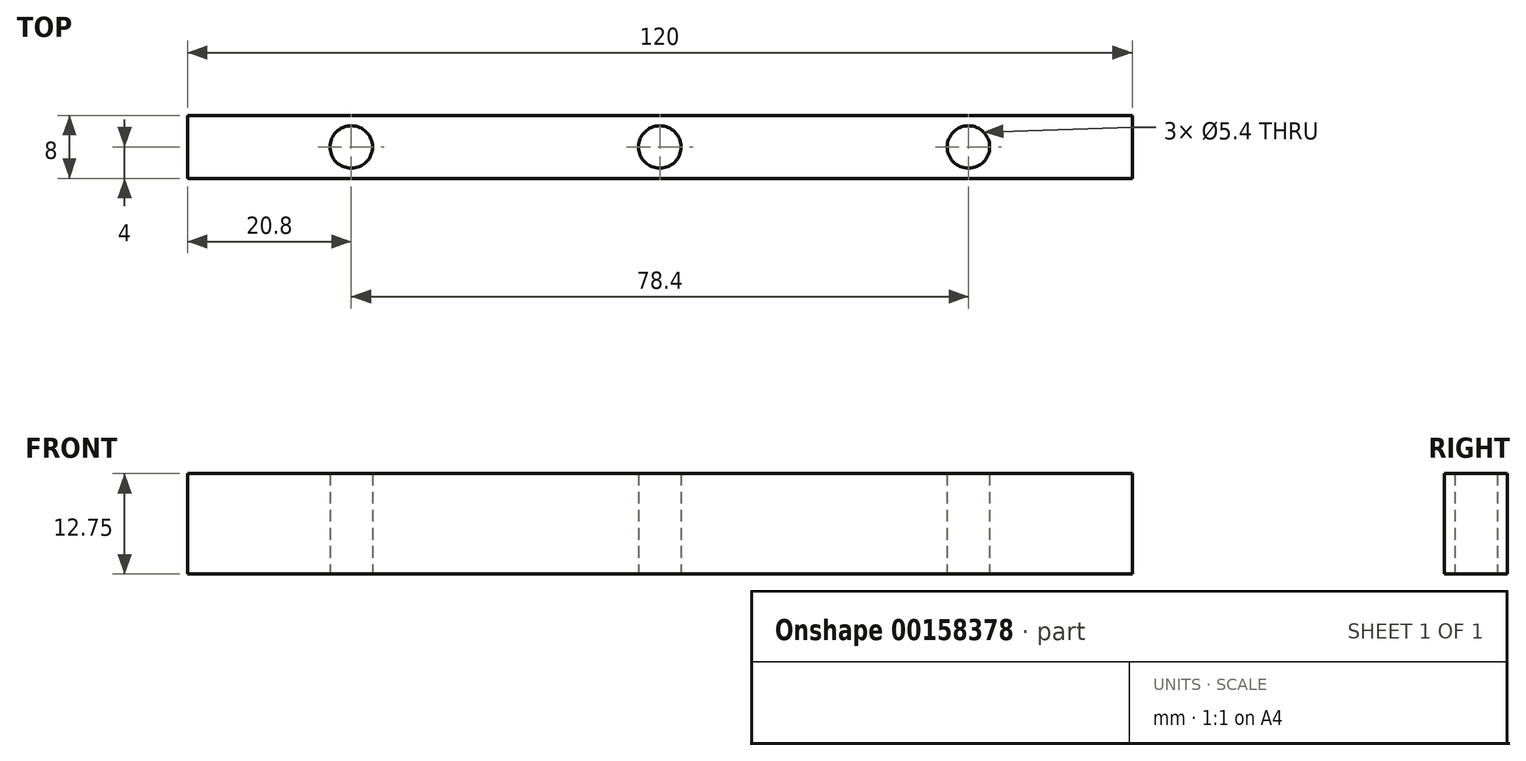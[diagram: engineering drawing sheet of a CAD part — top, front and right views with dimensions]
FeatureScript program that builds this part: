
annotation { "Feature Type Name" : "Feature", "Feature Type Description" : "" }
export const myFeature = defineFeature(function(context is Context, id is Id, definition is map)
    precondition{}
    {
        {
            var Q0;
            Q0=qCreatedBy(makeId("Top.planeOp"),FACE);
            var sketch = newSketch(context, id + "F0", { "sketchPlane" : qUnion([Q0])});
            skLineSegment(sketch, "E0.bottom", {"start": v(60, -4) * mm, "end": v(-60, -4) * mm});
            skLineSegment(sketch, "E0.top", {"start": v(60, 4) * mm, "end": v(-60, 4) * mm});
            skLineSegment(sketch, "E0.left", {"start": v(60, -4) * mm, "end": v(60, 4) * mm});
            skLineSegment(sketch, "E0.right", {"start": v(-60, -4) * mm, "end": v(-60, 4) * mm});
            skPoint(sketch, "E0.middle", {"position": v(0, 0) * mm});
            skCircle(sketch, "E1", {"center": v(-39.2, 0) * mm, "radius": 2.7 * mm});
            skCircle(sketch, "E2", {"center": v(0, 0) * mm, "radius": 2.7 * mm});
            skCircle(sketch, "E3", {"center": v(39.2, 0) * mm, "radius": 2.7 * mm});
            skSolve(sketch);
        }
        {
            var Q0;
            Q0 = qSketchRegion(id + "F0", true);
            extrude(context, id + "F1", {"entities" : qUnion([Q0]), "depth" : 12.75 * mm});
        }
    });
